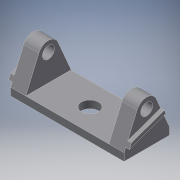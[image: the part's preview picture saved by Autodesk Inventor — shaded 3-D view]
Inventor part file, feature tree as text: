
AUTODESK INVENTOR PART (.ipt)
format: ipt  version: 2019 (Build 230136000, 136)  size: 157,696 bytes
history: native  units: in
note: dims shown in document units (in); Inventor stores cm internally (conversion verified against a paired STEP export)
features: sketch x4, extrude x3, other x3, mirror x2, hole x1, reference x1
ambient origin geometry x8: Origin, YZ Plane, XZ Plane, XY Plane, X Axis, Y Axis, Z Axis, Center Point
bodies: Solid1 (feature_tree)
feature tree (14):
  extrude  "Extrusion1"  Depth=1.1811in
  extrude  "Extrusion2"  Depth=0.0787in
  mirror  "Mirror1"
  extrude  "Extrusion5"  Depth=0.2756in
  mirror  "Mirror2"
  hole  "Hole1"  [1 undecoded]
  sketch  "Sketch1"  dims[d0=0.4724in d1=1.1811in]
  sketch  "Sketch2"  dims[d2=0.0787in d3=0.0in d4=0.125in]
  sketch  "Sketch5"  dims[d5=0.2165in d6=0.2756in]
  reference  "Reference4"
  sketch  "Sketch6"  dims[d7=0.1575in d8=0.0in d16=0.0394in d17=0.0394in d18=0.0in d23=0.0394in d24=0.1184in d25=0.177in d26=0.146in d27=0.332in d28=0.0787in d29=0.5635in d30=0.2241in d31=0.8108in]
  other  "<userpath>\Documents\IQC\PolarizationMethod.iam"
  other  "PolarizationMethod.iam"
  other  "FiberMount:1"
note: 1 required parameter value undecoded (feature->parameter linkage not recoverable at this tier; creation-order binding heuristic only, values carry confidence <= 0.55)
